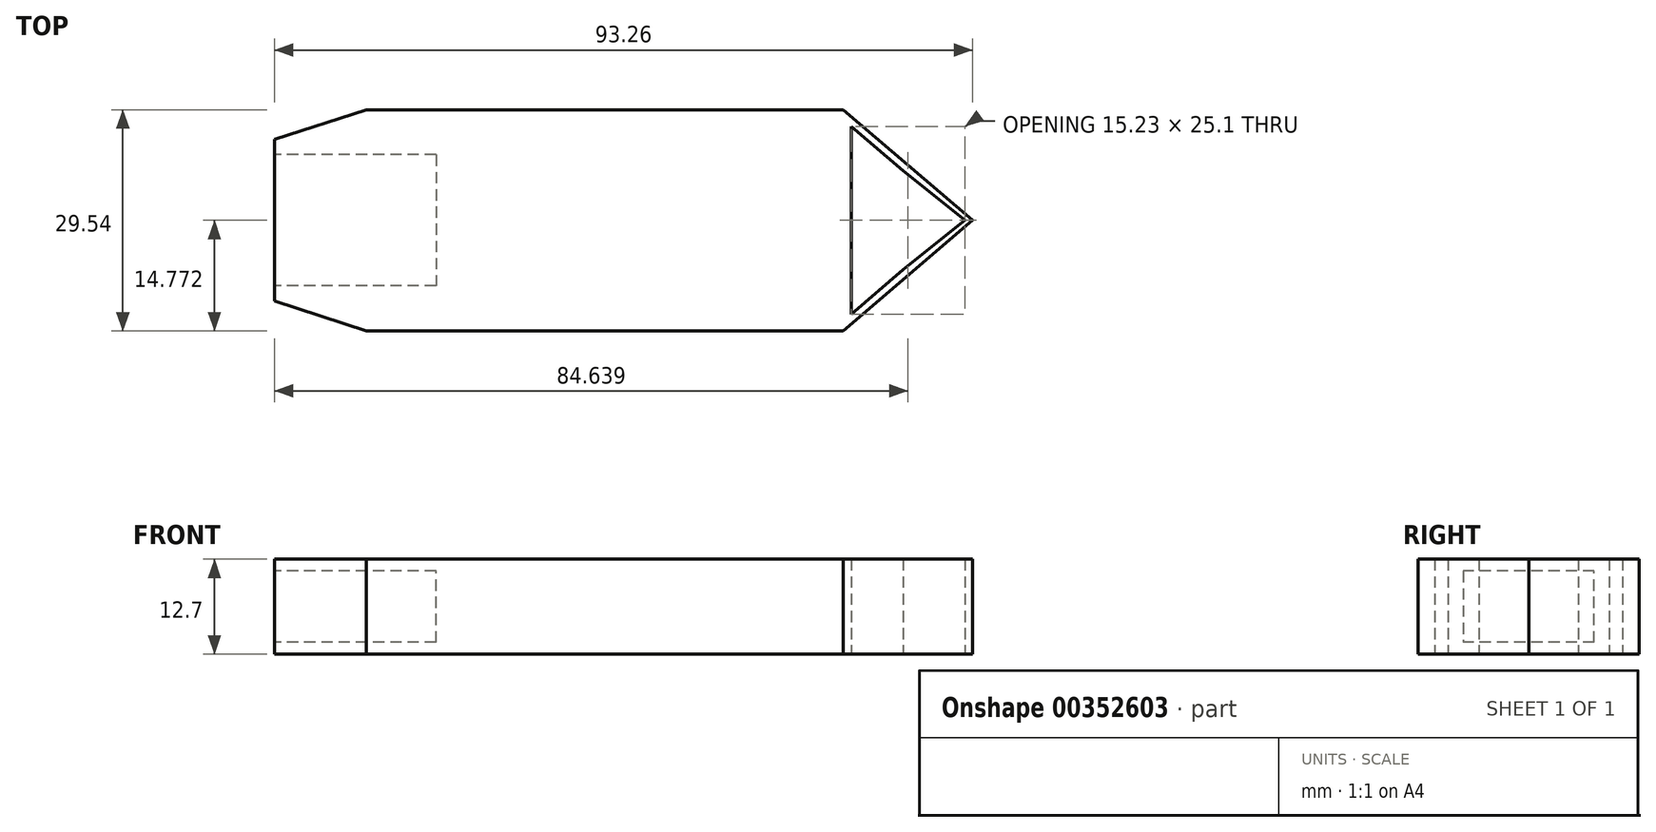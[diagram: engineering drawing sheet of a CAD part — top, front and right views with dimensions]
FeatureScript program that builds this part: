
annotation { "Feature Type Name" : "Feature", "Feature Type Description" : "" }
export const myFeature = defineFeature(function(context is Context, id is Id, definition is map)
    precondition{}
    {
        {
            var Q0;
            Q0=qCreatedBy(makeId("Top.planeOp"),FACE);
            var sketch = newSketch(context, id + "F0", { "sketchPlane" : qUnion([Q0])});
            skLineSegment(sketch, "E0", {"start": v(50.47, 6.61) * mm, "end": v(33.2, 21.38) * mm});
            skLineSegment(sketch, "E1", {"start": v(50.47, 6.61) * mm, "end": v(33.2, -8.16) * mm});
            skLineSegment(sketch, "E2", {"start": v(33.2, -8.16) * mm, "end": v(33.2, 21.38) * mm});
            skLineSegment(sketch, "E3", {"start": v(33.2, -8.16) * mm, "end": v(-30.5, -8.16) * mm});
            skLineSegment(sketch, "E4", {"start": v(33.2, 21.38) * mm, "end": v(-30.5, 21.38) * mm});
            skLineSegment(sketch, "E5", {"start": v(-30.5, 21.38) * mm, "end": v(-42.79, 17.4) * mm});
            skLineSegment(sketch, "E6.MirrorCS", {"start": v(-30.5, -8.16) * mm, "end": v(-42.79, -4.17) * mm});
            skLineSegment(sketch, "E7", {"start": v(-42.79, 17.4) * mm, "end": v(-42.79, -4.17) * mm});
            skPoint(sketch, "E8.0.midPoint", {"position": v(38.82, 6.17) * mm});
            skLineSegment(sketch, "E9", {"start": v(41.18, 0) * mm, "end": v(34.24, -5.94) * mm});
            skLineSegment(sketch, "E10", {"start": v(34.24, 6.61) * mm, "end": v(34.24, -5.94) * mm});
            skLineSegment(sketch, "E11.MirrorCS", {"start": v(34.24, 6.61) * mm, "end": v(34.24, 19.16) * mm});
            skLineSegment(sketch, "E12.MirrorCS", {"start": v(41.18, 13.22) * mm, "end": v(34.24, 19.16) * mm});
            skLineSegment(sketch, "E13", {"start": v(49.46, 6.61) * mm, "end": v(41.18, 13.22) * mm});
            skLineSegment(sketch, "E14", {"start": v(49.46, 6.61) * mm, "end": v(41.18, 0) * mm});
            skSolve(sketch);
        }
        {
            var Q0;
            Q0=makeQuery(id+"F0.imprint","IMPRINT",FACE,{"disambiguationData":[TD([[makeQuery(id+"F0.imprint","IMPRINT",EDGE,{"derivedFrom":sQuery(id+"F0.wireOp",EDGE,"E2")}),1.0]])]});
            var Q1;
            Q1=makeQuery(id+"F0.imprint","IMPRINT",FACE,{"disambiguationData":[TD([[makeQuery(id+"F0.imprint","IMPRINT",EDGE,{"derivedFrom":sQuery(id+"F0.wireOp",EDGE,"E0")}),1.0]])]});
            extrude(context, id + "F1", {"entities" : qUnion([Q0, Q1]), "depth" : 12.7 * mm});
        }
        {
            var Q0;
            Q0=makeQuery(id+"F1.opExtrude","SWEPT_FACE",FACE,{"disambiguationData":[OSD([sQuery(id+"F0.wireOp",EDGE,"E7")])]});
            var sketch = newSketch(context, id + "F2", { "sketchPlane" : qUnion([Q0])});
            skLineSegment(sketch, "E15", {"start": v(-15.37, 6.35) * mm, "end": v(-15.37, 11.1) * mm});
            skLineSegment(sketch, "E16.MirrorCS", {"start": v(-15.37, 6.35) * mm, "end": v(-15.37, 1.6) * mm});
            skLineSegment(sketch, "E17.MirrorCS", {"start": v(2.14, 6.35) * mm, "end": v(2.14, 11.1) * mm});
            skLineSegment(sketch, "E18.MirrorCS", {"start": v(2.14, 6.35) * mm, "end": v(2.14, 1.6) * mm});
            skLineSegment(sketch, "E19", {"start": v(-15.37, 11.1) * mm, "end": v(2.14, 11.1) * mm});
            skLineSegment(sketch, "E20", {"start": v(-15.37, 1.6) * mm, "end": v(2.14, 1.6) * mm});
            skSolve(sketch);
        }
        {
            var Q0;
            Q0=makeQuery(id+"F2.imprint","IMPRINT",FACE,{"disambiguationData":[TD([[makeQuery(id+"F2.imprint","IMPRINT",EDGE,{"derivedFrom":sQuery(id+"F2.wireOp",EDGE,"E15")}),-1.0]])]});
            extrude(context, id + "F3", {"entities" : qUnion([Q0]), "operationType" : NewBodyOperationType.REMOVE, "oppositeDirection" : true, "depth" : 21.59 * mm});
        }
    });
